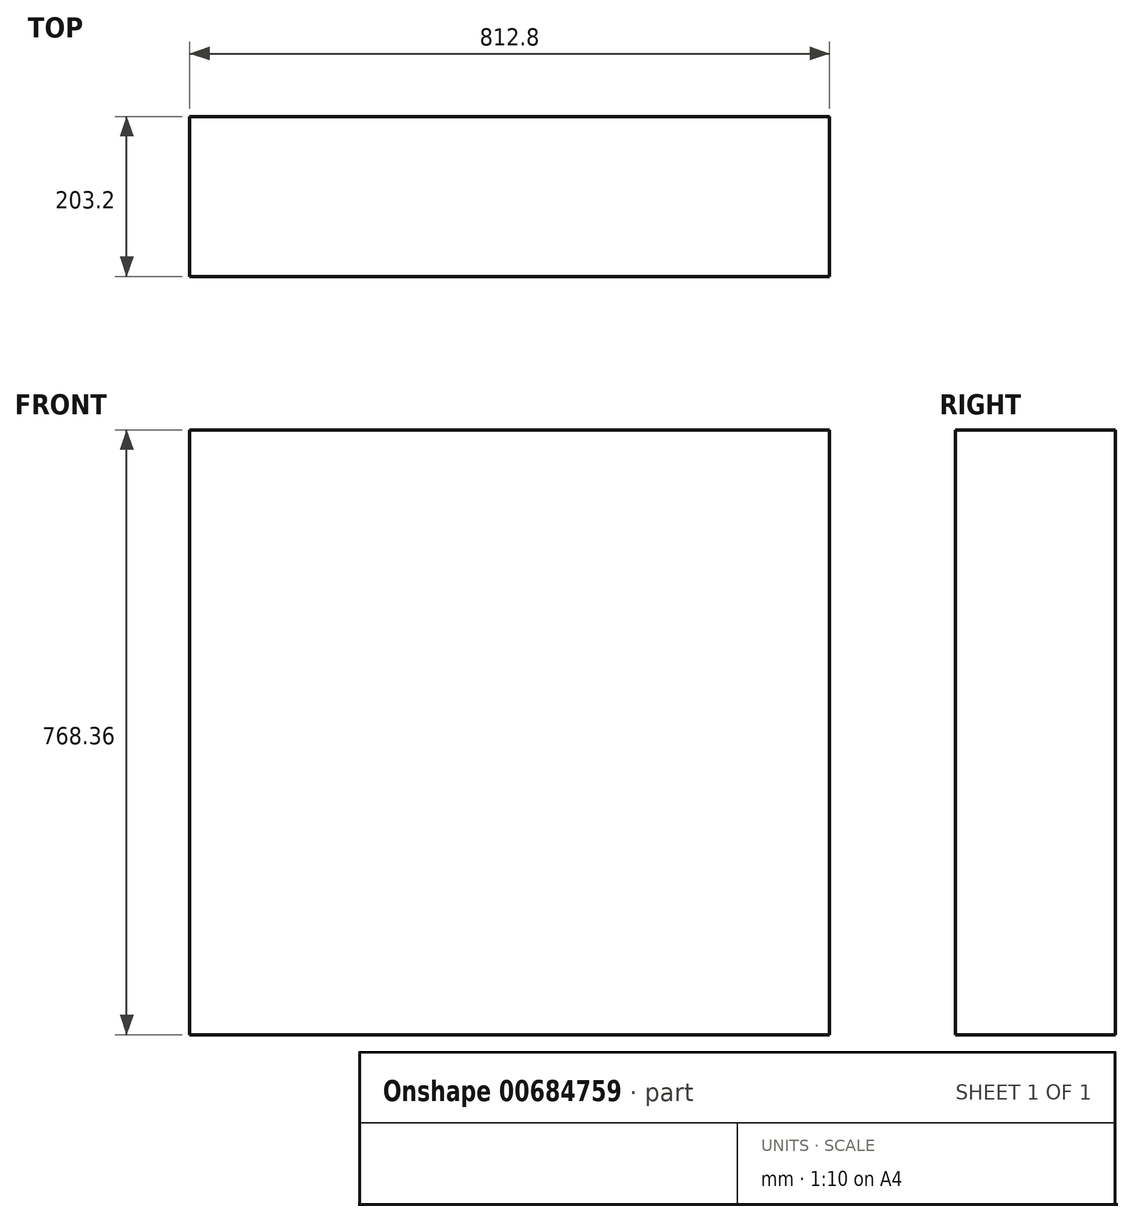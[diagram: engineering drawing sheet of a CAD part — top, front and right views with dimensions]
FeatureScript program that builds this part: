
annotation { "Feature Type Name" : "Feature", "Feature Type Description" : "" }
export const myFeature = defineFeature(function(context is Context, id is Id, definition is map)
    precondition{}
    {
        {
            var Q0;
            Q0=qCreatedBy(makeId("Right.planeOp"),FACE);
            var sketch = newSketch(context, id + "F0", { "sketchPlane" : qUnion([Q0])});
            skLineSegment(sketch, "E0.bottom", {"start": v(-101.6, 384.18) * mm, "end": v(101.6, 384.18) * mm});
            skLineSegment(sketch, "E0.top", {"start": v(-101.6, -384.18) * mm, "end": v(101.6, -384.18) * mm});
            skLineSegment(sketch, "E0.left", {"start": v(-101.6, 384.18) * mm, "end": v(-101.6, -384.18) * mm});
            skLineSegment(sketch, "E0.right", {"start": v(101.6, 384.18) * mm, "end": v(101.6, -384.18) * mm});
            skLineSegment(sketch, "E1", {"start": v(101.6, 384.18) * mm, "end": v(-101.6, -384.18) * mm, "construction": true});
            skSolve(sketch);
        }
        {
            var Q0;
            Q0=qSketchRegion(id+"F0",true);
            extrude(context, id + "F1", {"entities" : qUnion([Q0]), "endBound" : BoundingType.SYMMETRIC, "depth" : 812.8 * mm, "offsetDistance" : 25.4 * mm});
        }
    });
